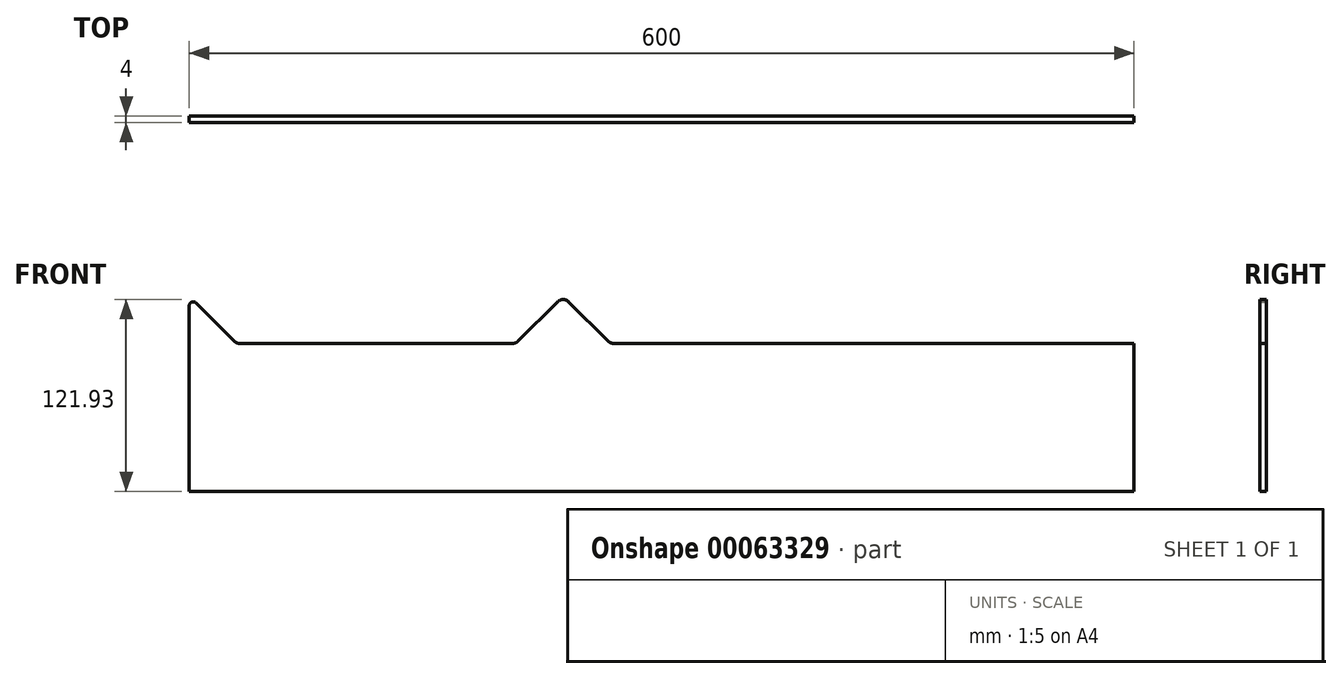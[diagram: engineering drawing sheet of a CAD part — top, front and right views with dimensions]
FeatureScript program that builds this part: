
annotation { "Feature Type Name" : "Feature", "Feature Type Description" : "" }
export const myFeature = defineFeature(function(context is Context, id is Id, definition is map)
    precondition{}
    {
        {
            var Q0;
            Q0=qCreatedBy(makeId("Front.planeOp"),FACE);
            var sketch = newSketch(context, id + "F0", { "sketchPlane" : qUnion([Q0])});
            skLineSegment(sketch, "E0.rect.top", {"start": v(-220, -62) * mm, "end": v(280, -62) * mm});
            skLineSegment(sketch, "E0.rect.left", {"start": v(-270, 55.96) * mm, "end": v(-270, 18) * mm});
            skPoint(sketch, "E0.rect.middle", {"position": v(0, 0) * mm});
            skLineSegment(sketch, "E1", {"start": v(-265.73, 57.73) * mm, "end": v(-241.46, 33.46) * mm});
            skLineSegment(sketch, "E2", {"start": v(-237.93, 32) * mm, "end": v(-64.57, 32) * mm});
            skPoint(sketch, "E3.orphan", {"position": v(270, 62) * mm});
            skLineSegment(sketch, "E4.bottom", {"start": v(265, 32) * mm, "end": v(285, 32) * mm});
            skLineSegment(sketch, "E5", {"start": v(-3.96, 33.46) * mm, "end": v(-28.96, 58.46) * mm});
            skLineSegment(sketch, "E6", {"start": v(-36.04, 58.46) * mm, "end": v(-61.04, 33.46) * mm});
            skLineSegment(sketch, "E7.top", {"start": v(-270, 18) * mm, "end": v(-220, 18) * mm});
            skLineSegment(sketch, "E7.right", {"start": v(-220, -62) * mm, "end": v(-220, 18) * mm});
            skPoint(sketch, "E8.orphan", {"position": v(-270, -62) * mm});
            skLineSegment(sketch, "E9.top", {"start": v(330, 18) * mm, "end": v(280, 18) * mm});
            skLineSegment(sketch, "E9.right", {"start": v(280, -62) * mm, "end": v(280, 18) * mm});
            skPoint(sketch, "E9.bottom.end.orphan", {"position": v(270, -62) * mm});
            skPoint(sketch, "E10.visualSharp", {"position": v(-270, 62) * mm});
            skArc(sketch, "E10.filletArc", {"start": v(-265.73, 57.73) * mm, "mid": v(-268.46, 58.27) * mm, "end": v(-270, 55.96) * mm});
            skPoint(sketch, "E11.visualSharp", {"position": v(-240, 32) * mm});
            skArc(sketch, "E11.filletArc", {"start": v(-241.46, 33.46) * mm, "mid": v(-239.84, 32.38) * mm, "end": v(-237.93, 32) * mm});
            skPoint(sketch, "E12.newPointA", {"position": v(265, 32) * mm});
            skPoint(sketch, "E12.newPointB", {"position": v(-62.5, 32) * mm});
            skArc(sketch, "E12.filletArc", {"start": v(-64.57, 32) * mm, "mid": v(-62.66, 32.38) * mm, "end": v(-61.04, 33.46) * mm});
            skPoint(sketch, "E13.visualSharp", {"position": v(-32.5, 62) * mm});
            skArc(sketch, "E13.filletArc", {"start": v(-28.96, 58.46) * mm, "mid": v(-32.5, 59.93) * mm, "end": v(-36.04, 58.46) * mm});
            skLineSegment(sketch, "E14", {"start": v(-0.43, 32) * mm, "end": v(265, 32) * mm});
            skPoint(sketch, "E15.visualSharp", {"position": v(-2.5, 32) * mm});
            skArc(sketch, "E15.filletArc", {"start": v(-3.96, 33.46) * mm, "mid": v(-2.34, 32.38) * mm, "end": v(-0.43, 32) * mm});
            skLineSegment(sketch, "E16.bottom", {"start": v(285, 32) * mm, "end": v(330, 32) * mm});
            skLineSegment(sketch, "E16.top", {"start": v(285, 17) * mm, "end": v(330, 17) * mm});
            skLineSegment(sketch, "E16.right", {"start": v(330, 32) * mm, "end": v(330, 17) * mm});
            skLineSegment(sketch, "E17.0", {"start": v(-237.93, 33) * mm, "end": v(-62.91, 33) * mm});
            skLineSegment(sketch, "E17.1", {"start": v(-2.09, 33) * mm, "end": v(265, 33) * mm});
            skLineSegment(sketch, "E17.2", {"start": v(-2.09, 33) * mm, "end": v(-28.26, 59.17) * mm});
            skArc(sketch, "E17.3", {"start": v(-28.26, 59.17) * mm, "mid": v(-32.5, 60.93) * mm, "end": v(-36.74, 59.17) * mm});
            skLineSegment(sketch, "E17.4", {"start": v(-36.74, 59.17) * mm, "end": v(-62.91, 33) * mm});
            skLineSegment(sketch, "E18.0", {"start": v(-265.03, 58.44) * mm, "end": v(-240.76, 34.17) * mm});
            skArc(sketch, "E18.1", {"start": v(-265.03, 58.44) * mm, "mid": v(-268.84, 59.2) * mm, "end": v(-271, 55.96) * mm});
            skLineSegment(sketch, "E19.0", {"start": v(265, 33) * mm, "end": v(285, 33) * mm});
            skLineSegment(sketch, "E20.0", {"start": v(285, 33) * mm, "end": v(330, 33) * mm});
            skLineSegment(sketch, "E21.bottom", {"start": v(-270, 18) * mm, "end": v(-270, 18) * mm});
            skLineSegment(sketch, "E21.top", {"start": v(-270, -62) * mm, "end": v(-270, -62) * mm});
            skLineSegment(sketch, "E21.left", {"start": v(-270, 18) * mm, "end": v(-270, -62) * mm});
            skLineSegment(sketch, "E21.right", {"start": v(-270, 18) * mm, "end": v(-270, -62) * mm});
            skLineSegment(sketch, "E22.bottom", {"start": v(-220, -62) * mm, "end": v(-270, -62) * mm});
            skLineSegment(sketch, "E22.top", {"start": v(-220, -62) * mm, "end": v(-270, -62) * mm});
            skLineSegment(sketch, "E22.left", {"start": v(-220, -62) * mm, "end": v(-220, -62) * mm});
            skLineSegment(sketch, "E23.bottom", {"start": v(280, -62) * mm, "end": v(330, -62) * mm});
            skLineSegment(sketch, "E23.top", {"start": v(280, 18) * mm, "end": v(330, 18) * mm});
            skLineSegment(sketch, "E23.right", {"start": v(330, -62) * mm, "end": v(330, 18) * mm});
            skSolve(sketch);
        }
        {
            var Q0;
            Q0 = qSketchRegion(id + "F0", true);
            var Q1;
            Q1=makeQuery(id+"F0.imprint","IMPRINT",FACE,{"disambiguationData":[TD([[makeQuery(id+"F0.imprint","IMPRINT",EDGE,{"derivedFrom":sQuery(id+"F0.wireOp",EDGE,"E0.rect.top")}),1.0]])]});
            extrude(context, id + "F1", {"entities" : qUnion([Q0, Q1]), "depth" : 4 * mm});
        }
    });
